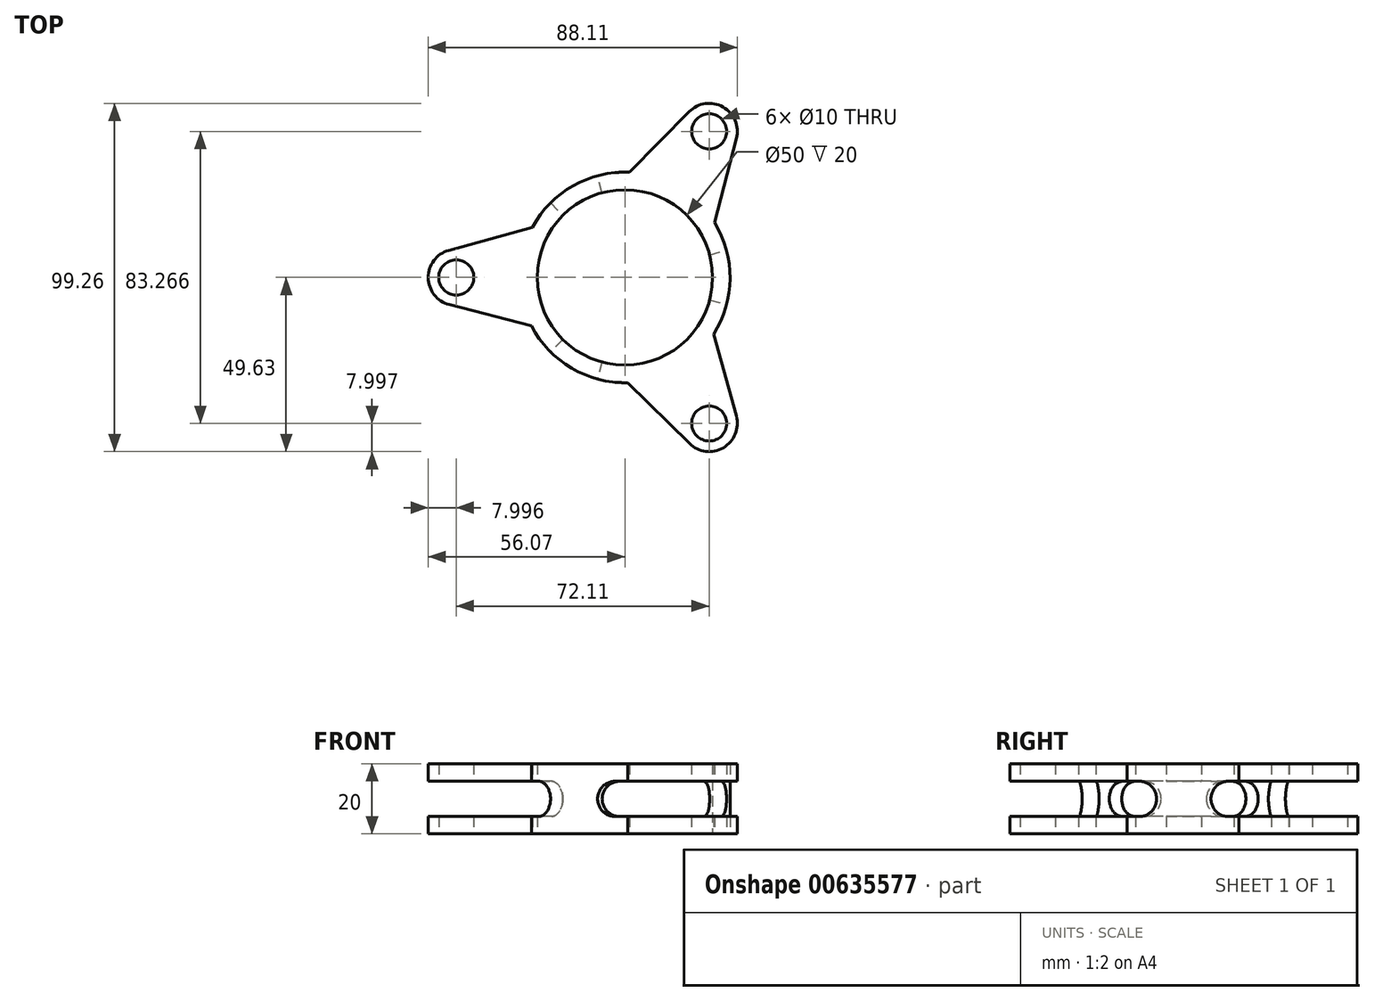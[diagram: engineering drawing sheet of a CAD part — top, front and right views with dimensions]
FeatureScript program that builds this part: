
annotation { "Feature Type Name" : "Feature", "Feature Type Description" : "" }
export const myFeature = defineFeature(function(context is Context, id is Id, definition is map)
    precondition{}
    {
        {
            var Q0;
            Q0=qCreatedBy(makeId("Top.planeOp"),FACE);
            var sketch = newSketch(context, id + "F0", { "sketchPlane" : qUnion([Q0])});
            skCircle(sketch, "E0", {"center": v(0, 0) * mm, "radius": 30 * mm});
            skLineSegment(sketch, "E1", {"start": v(-50.2, 7.71) * mm, "end": v(-26.37, 14.3) * mm});
            skLineSegment(sketch, "E2", {"start": v(-50.08, -7.74) * mm, "end": v(-26.63, -13.82) * mm});
            skPoint(sketch, "E3.visualSharp", {"position": v(-78.98, -0.26) * mm});
            skArc(sketch, "E3.filletArc", {"start": v(-50.2, 7.71) * mm, "mid": v(-56.07, -0.07) * mm, "end": v(-50.08, -7.74) * mm});
            skLineSegment(sketch, "E4.1.0", {"start": v(18.43, -47.34) * mm, "end": v(0.8, -29.99) * mm});
            skArc(sketch, "E4.1.1", {"start": v(18.43, -47.34) * mm, "mid": v(28.1, -48.53) * mm, "end": v(31.75, -39.5) * mm});
            skLineSegment(sketch, "E4.1.2", {"start": v(31.75, -39.5) * mm, "end": v(25.28, -16.15) * mm});
            skLineSegment(sketch, "E4.2.0", {"start": v(31.78, 39.63) * mm, "end": v(25.58, 15.68) * mm});
            skArc(sketch, "E4.2.1", {"start": v(31.78, 39.63) * mm, "mid": v(27.98, 48.6) * mm, "end": v(18.33, 47.24) * mm});
            skLineSegment(sketch, "E4.2.2", {"start": v(18.33, 47.24) * mm, "end": v(1.34, 29.97) * mm});
            skCircle(sketch, "E5", {"center": v(-48.07, 0) * mm, "radius": 5 * mm});
            skCircle(sketch, "E6", {"center": v(0, 0) * mm, "radius": 25 * mm});
            skCircle(sketch, "E7", {"center": v(24.04, 41.63) * mm, "radius": 5 * mm});
            skCircle(sketch, "E8", {"center": v(24.04, -41.63) * mm, "radius": 5 * mm});
            skSolve(sketch);
        }
        {
            var Q0;
            Q0 = qSketchRegion(id + "F0", true);
            extrude(context, id + "F1", {"entities" : qUnion([Q0]), "depth" : 10 * mm, "offsetDistance" : 25 * mm, "hasSecondDirection" : true, "secondDirectionOppositeDirection" : true, "secondDirectionDepth" : 10 * mm});
        }
        {
            var Q0;
            Q0=qCreatedBy(makeId("Front.planeOp"),FACE);
            var sketch = newSketch(context, id + "F2", { "sketchPlane" : qUnion([Q0])});
            skLineSegment(sketch, "E9", {"start": v(0, 0) * mm, "end": v(-69.94, 0) * mm});
            skLineSegment(sketch, "E10.bottom", {"start": v(0.03, 5) * mm, "end": v(-69.97, 5) * mm});
            skLineSegment(sketch, "E10.top", {"start": v(0.03, -5) * mm, "end": v(-69.97, -5) * mm});
            skLineSegment(sketch, "E10.left", {"start": v(0.03, 5) * mm, "end": v(0.03, -5) * mm});
            skLineSegment(sketch, "E10.right", {"start": v(-69.97, 5) * mm, "end": v(-69.97, -5) * mm});
            skPoint(sketch, "E10.middle", {"position": v(-34.97, 0) * mm});
            skSolve(sketch);
        }
        {
            var Q0;
            Q0=makeQuery(id+"F2.imprint","IMPRINT",FACE,{"disambiguationData":[TD([[makeQuery(id+"F2.imprint","IMPRINT",EDGE,{"derivedFrom":sQuery(id+"F2.wireOp",EDGE,"E10.bottom")}),1.0]])]});
            var Q1;
            Q1=sQuery(id+"F2.wireOp",EDGE,"E10.left");
            revolve(context, id + "F3", {"entities" : qUnion([Q0]), "axis" : qUnion([Q1]), "revolveType" : RevolveType.TWO_DIRECTIONS, "angle" : 45 * degree, "angleBack" : 315 * degree});
        }
        {
            var Q0;
            Q0=makeQuery(id+"F3.opRevolve","SWEPT_BODY",BODY,{"disambiguationData":[OSD([sQuery(id+"F2.wireOp",EDGE,"E10.bottom"),sQuery(id+"F2.wireOp",EDGE,"E10.top"),sQuery(id+"F2.wireOp",EDGE,"E10.left"),sQuery(id+"F2.wireOp",EDGE,"E10.right")])]});
            var Q1;
            Q1=makeQuery(id+"F1.opExtrude","CAP_EDGE",EDGE,{"disambiguationData":[OSD([sQuery(id+"F0.wireOp",EDGE,"E6")])],"isStart":false});
            circularPattern(context, id + "F4", {"entities" : qUnion([Q0]), "axis" : qUnion([Q1]), "angle" : 120 * degree, "instanceCount" : 3, "oppositeDirection" : true});
        }
        {
            var Q0;
            Q0=makeQuery(id+"F3.opRevolve","SWEPT_BODY",BODY,{"disambiguationData":[OSD([sQuery(id+"F2.wireOp",EDGE,"E10.bottom"),sQuery(id+"F2.wireOp",EDGE,"E10.top"),sQuery(id+"F2.wireOp",EDGE,"E10.left"),sQuery(id+"F2.wireOp",EDGE,"E10.right")])]});
            var Q1;
            Q1=makeQuery(id+"F4.opPattern","COPY",BODY,{"derivedFrom":makeQuery(id+"F3.opRevolve","SWEPT_BODY",BODY,{"disambiguationData":[OSD([sQuery(id+"F2.wireOp",EDGE,"E10.bottom"),sQuery(id+"F2.wireOp",EDGE,"E10.top"),sQuery(id+"F2.wireOp",EDGE,"E10.left"),sQuery(id+"F2.wireOp",EDGE,"E10.right")])]}),"instanceName":"1"});
            var Q2;
            Q2=makeQuery(id+"F4.opPattern","COPY",BODY,{"derivedFrom":makeQuery(id+"F3.opRevolve","SWEPT_BODY",BODY,{"disambiguationData":[OSD([sQuery(id+"F2.wireOp",EDGE,"E10.bottom"),sQuery(id+"F2.wireOp",EDGE,"E10.top"),sQuery(id+"F2.wireOp",EDGE,"E10.left"),sQuery(id+"F2.wireOp",EDGE,"E10.right")])]}),"instanceName":"2"});
            var Q3;
            Q3=makeQuery(id+"F1.opExtrude","SWEPT_BODY",BODY,{"disambiguationData":[OSD([sQuery(id+"F0.wireOp",EDGE,"E0"),sQuery(id+"F0.wireOp",EDGE,"E1"),sQuery(id+"F0.wireOp",EDGE,"E2"),sQuery(id+"F0.wireOp",EDGE,"E3.filletArc"),sQuery(id+"F0.wireOp",EDGE,"E4.1.0"),sQuery(id+"F0.wireOp",EDGE,"E4.1.1"),sQuery(id+"F0.wireOp",EDGE,"E4.1.2"),sQuery(id+"F0.wireOp",EDGE,"E4.2.0"),sQuery(id+"F0.wireOp",EDGE,"E4.2.1"),sQuery(id+"F0.wireOp",EDGE,"E4.2.2"),sQuery(id+"F0.wireOp",EDGE,"E5"),sQuery(id+"F0.wireOp",EDGE,"E6"),sQuery(id+"F0.wireOp",EDGE,"E7"),sQuery(id+"F0.wireOp",EDGE,"E8")])]});
            booleanBodies(context, id + "F5", {"operationType" : BooleanOperationType.SUBTRACTION, "tools" : qUnion([Q0, Q1, Q2]), "targets" : qUnion([Q3])});
        }
        {
            var Q0;
            Q0=makeQuery(id+"F5.opBoolean","COPY",EDGE,{"derivedFrom":makeQuery(id+"F4.opPattern","COPY",EDGE,{"derivedFrom":makeQuery(id+"F3.opRevolve","CAP_EDGE",EDGE,{"disambiguationData":[OSD([sQuery(id+"F2.wireOp",EDGE,"E10.bottom")])],"isStart":false}),"instanceName":"1"})});
            var Q1;
            Q1=makeQuery(id+"F5.opBoolean","COPY",EDGE,{"derivedFrom":makeQuery(id+"F4.opPattern","COPY",EDGE,{"derivedFrom":makeQuery(id+"F3.opRevolve","CAP_EDGE",EDGE,{"disambiguationData":[OSD([sQuery(id+"F2.wireOp",EDGE,"E10.top")])],"isStart":false}),"instanceName":"1"})});
            var Q2;
            Q2=makeQuery(id+"F5.opBoolean","COPY",EDGE,{"derivedFrom":makeQuery(id+"F4.opPattern","COPY",EDGE,{"derivedFrom":makeQuery(id+"F3.opRevolve","CAP_EDGE",EDGE,{"disambiguationData":[OSD([sQuery(id+"F2.wireOp",EDGE,"E10.top")])],"isStart":true}),"instanceName":"2"})});
            var Q3;
            Q3=makeQuery(id+"F5.opBoolean","COPY",EDGE,{"derivedFrom":makeQuery(id+"F4.opPattern","COPY",EDGE,{"derivedFrom":makeQuery(id+"F3.opRevolve","CAP_EDGE",EDGE,{"disambiguationData":[OSD([sQuery(id+"F2.wireOp",EDGE,"E10.bottom")])],"isStart":true}),"instanceName":"2"})});
            var Q4;
            Q4=makeQuery(id+"F5.opBoolean","COPY",EDGE,{"derivedFrom":makeQuery(id+"F4.opPattern","COPY",EDGE,{"derivedFrom":makeQuery(id+"F3.opRevolve","CAP_EDGE",EDGE,{"disambiguationData":[OSD([sQuery(id+"F2.wireOp",EDGE,"E10.bottom")])],"isStart":false}),"instanceName":"2"})});
            var Q5;
            Q5=makeQuery(id+"F5.opBoolean","COPY",EDGE,{"derivedFrom":makeQuery(id+"F4.opPattern","COPY",EDGE,{"derivedFrom":makeQuery(id+"F3.opRevolve","CAP_EDGE",EDGE,{"disambiguationData":[OSD([sQuery(id+"F2.wireOp",EDGE,"E10.top")])],"isStart":false}),"instanceName":"2"})});
            var Q6;
            Q6=makeQuery(id+"F5.opBoolean","COPY",EDGE,{"derivedFrom":makeQuery(id+"F3.opRevolve","CAP_EDGE",EDGE,{"disambiguationData":[OSD([sQuery(id+"F2.wireOp",EDGE,"E10.top")])],"isStart":false})});
            var Q7;
            Q7=makeQuery(id+"F5.opBoolean","COPY",EDGE,{"derivedFrom":makeQuery(id+"F4.opPattern","COPY",EDGE,{"derivedFrom":makeQuery(id+"F3.opRevolve","CAP_EDGE",EDGE,{"disambiguationData":[OSD([sQuery(id+"F2.wireOp",EDGE,"E10.top")])],"isStart":true}),"instanceName":"1"})});
            var Q8;
            Q8=makeQuery(id+"F5.opBoolean","COPY",EDGE,{"derivedFrom":makeQuery(id+"F3.opRevolve","CAP_EDGE",EDGE,{"disambiguationData":[OSD([sQuery(id+"F2.wireOp",EDGE,"E10.bottom")])],"isStart":false})});
            var Q9;
            Q9=makeQuery(id+"F5.opBoolean","COPY",EDGE,{"derivedFrom":makeQuery(id+"F4.opPattern","COPY",EDGE,{"derivedFrom":makeQuery(id+"F3.opRevolve","CAP_EDGE",EDGE,{"disambiguationData":[OSD([sQuery(id+"F2.wireOp",EDGE,"E10.bottom")])],"isStart":true}),"instanceName":"1"})});
            var Q10;
            Q10=makeQuery(id+"F5.opBoolean","COPY",EDGE,{"derivedFrom":makeQuery(id+"F3.opRevolve","CAP_EDGE",EDGE,{"disambiguationData":[OSD([sQuery(id+"F2.wireOp",EDGE,"E10.top")])],"isStart":true})});
            var Q11;
            Q11=makeQuery(id+"F5.opBoolean","COPY",EDGE,{"derivedFrom":makeQuery(id+"F3.opRevolve","CAP_EDGE",EDGE,{"disambiguationData":[OSD([sQuery(id+"F2.wireOp",EDGE,"E10.bottom")])],"isStart":true})});
            fillet(context, id + "F6", {"entities" : qUnion([Q0, Q1, Q2, Q3, Q4, Q5, Q6, Q7, Q8, Q9, Q10, Q11]), "radius" : 5 * mm, "tangentPropagation" : true, "allowEdgeOverflow" : false});
        }
    });
